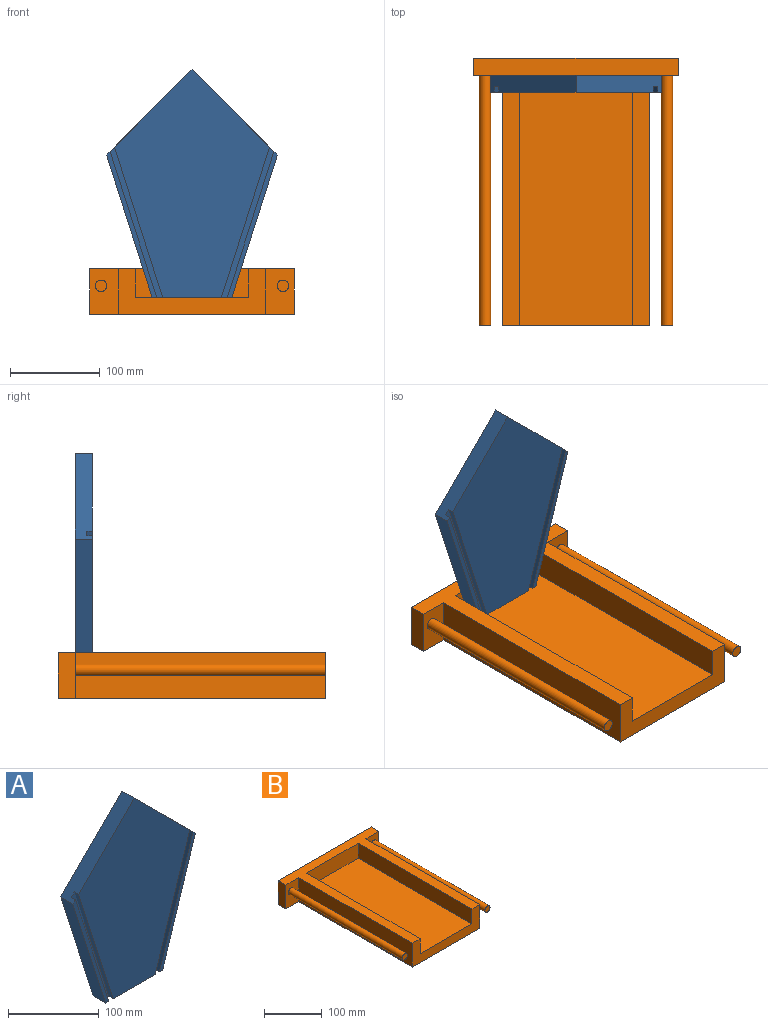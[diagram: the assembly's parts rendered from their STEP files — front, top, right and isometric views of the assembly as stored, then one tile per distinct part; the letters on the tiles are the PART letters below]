
ASSEMBLY  parts=2 mates=2
PART A: 15 faces, bbox 190.5x19.1x254 mm
  f0: plane 254x172.82mm, normal (0,-1,0), area 27442.3mm2, adj f2,f3,f5,f10,f13
  f1: plane 162.54x55.8mm, normal (0,-1,0), area 803.3mm2, adj f3,f4,f5,f12
  f2: plane 95.25x95.25mm, normal (0.71,0,0.71), area 2520.7mm2, adj f0,f3,f6,f7,f8,f9,f10,f11
  f3: plane 95.25x95.25mm, normal (-0.71,0,0.71), area 2520.7mm2, adj f0,f1,f2,f4,f8,f12,f13,f14
  f4: plane 158.75x50.8mm, normal (-0.95,0,-0.3), area 3175.3mm2, adj f1,f3,f5,f8
  f5: plane 88.9x19.05mm, normal (0,0,-1), area 1608.9mm2, adj f0,f1,f4,f6,f7,f8,f9,f10
  f6: plane 158.75x50.8mm, normal (0.95,0,-0.3), area 3175.3mm2, adj f2,f5,f7,f8
  f7: plane 162.54x55.8mm, normal (0,-1,0), area 803.3mm2, adj f2,f5,f6,f9
  f8: plane 254x190.5mm, normal (0,1,0), area 31249.9mm2, adj f2,f3,f4,f5,f6
  f9: plane 162.54x52.01mm, normal (-0.95,0,0.3), area 1083.7mm2, adj f2,f5,f7,f11
  f10: plane 167.59x53.63mm, normal (0.95,0,-0.3), area 1117.3mm2, adj f0,f2,f5,f11
  f11: plane 167.59x58.68mm, normal (0,-1,0), area 1100.5mm2, adj f2,f5,f9,f10
  f12: plane 162.54x52.01mm, normal (0.95,0,0.3), area 1083.7mm2, adj f1,f3,f5,f14
  f13: plane 167.59x53.63mm, normal (-0.95,0,-0.3), area 1117.3mm2, adj f0,f3,f5,f14
  f14: plane 167.59x58.68mm, normal (0,-1,0), area 1100.5mm2, adj f3,f5,f12,f13
PART B: 18 faces, bbox 228.6x298.5x50.8 mm
  f0: plane 127x31.75mm, normal (0,-1,0), area 4032.3mm2, adj f2,f14,f15,f16
  f1: plane 50.8x31.75mm, normal (0,-1,0), area 1486.2mm2, adj f2,f4,f5,f10,f13
  f2: plane 298.45x228.6mm, normal (0,0,1), area 15000mm2, adj f0,f1,f3,f5,f6,f7,f12,f13
  f3: plane 50.8x19.05mm, normal (-1,0,0), area 967.7mm2, adj f2,f4,f6,f7
  f4: plane 298.45x228.6mm, normal (0,0,-1), area 50483.8mm2, adj f1,f3,f5,f6,f7,f12,f13,f17
  f5: plane 50.8x19.05mm, normal (1,0,0), area 967.7mm2, adj f1,f2,f4,f7
  f6: plane 50.8x31.75mm, normal (0,-1,0), area 1486.2mm2, adj f2,f3,f4,f8,f12
  f7: plane 228.6x50.8mm, normal (0,1,0), area 11612.9mm2, adj f2,f3,f4,f5
  f8: cylinder r=6.35mm len=279.4mm, axis (0,1,0), area 11147.6mm2, adj f6,f9
  f9: plane 12.7x12.7mm, normal (0,-1,0), area 126.7mm2, adj f8
  f10: cylinder r=6.35mm len=279.4mm, axis (0,1,0), area 11147.6mm2, adj f1,f11
  f11: plane 12.7x12.7mm, normal (0,-1,0), area 126.7mm2, adj f10
  f12: plane 279.4x50.8mm, normal (-1,0,0), area 14193.5mm2, adj f2,f4,f6,f17
  f13: plane 279.4x50.8mm, normal (1,0,0), area 14193.5mm2, adj f1,f2,f4,f17
  f14: plane 279.4x31.75mm, normal (-1,0,0), area 8870.9mm2, adj f0,f2,f15,f17
  f15: plane 279.4x127mm, normal (0,0,1), area 35483.8mm2, adj f0,f14,f16,f17
  f16: plane 279.4x31.75mm, normal (1,0,0), area 8870.9mm2, adj f0,f2,f15,f17
  f17: plane 165.1x50.8mm, normal (0,-1,0), area 4354.8mm2, adj f2,f4,f12,f13,f14,f15,f16
PLACE A t=(21.97,177.49,37.16)mm
PLACE B t=(21.97,196.54,-83.49)mm
MATE planar A.f8 <-> B.f0  axis (0,1,0) through (21.97,177.49,-89.84)mm
MATE planar B.f15 <-> A.f5  axis (0,0,1) through (21.97,37.79,-89.84)mm
